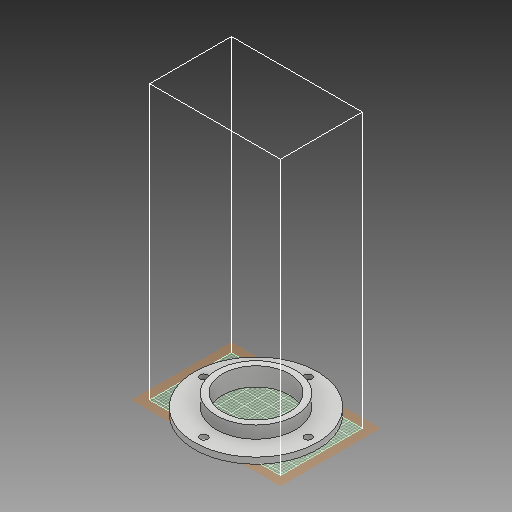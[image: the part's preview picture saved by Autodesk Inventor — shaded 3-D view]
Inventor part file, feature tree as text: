
AUTODESK INVENTOR PART (.ipt)
format: ipt  version: 2018 (Build 220112000, 112)  size: 478,720 bytes
history: native  units: mm
features: extrude x3, sketch x3, other x1, pattern_circular x1
ambient origin geometry x8: Origin, YZ Plane, XZ Plane, XY Plane, X Axis, Y Axis, Z Axis, Center Point
bodies: Body1 (feature_tree)
feature tree (8):
  other  "Sólido1"
  extrude  "Extrusión1"  Depth=3.0mm
  extrude  "Extrusión2"  Depth=6.0mm
  extrude  "Extrusión3"  Depth=3.0mm
  pattern_circular  "Patrón circular1"  [2 undecoded]
  sketch  "Boceto1"  dims[d0=32.52mm d1=3.0mm]
  sketch  "Boceto2"  dims[d2=6.0mm d3=0.0mm d4=60.0mm]
  sketch  "Boceto3"  dims[d5=3.0mm d6=0.0mm d7=3.0mm d8=25.5mm d9=60.0mm d11=3.0mm d12=0.0mm d13=40.0mm d14=360.0deg]
note: 2 required parameter values undecoded (feature->parameter linkage not recoverable at this tier; creation-order binding heuristic only, values carry confidence <= 0.55)
